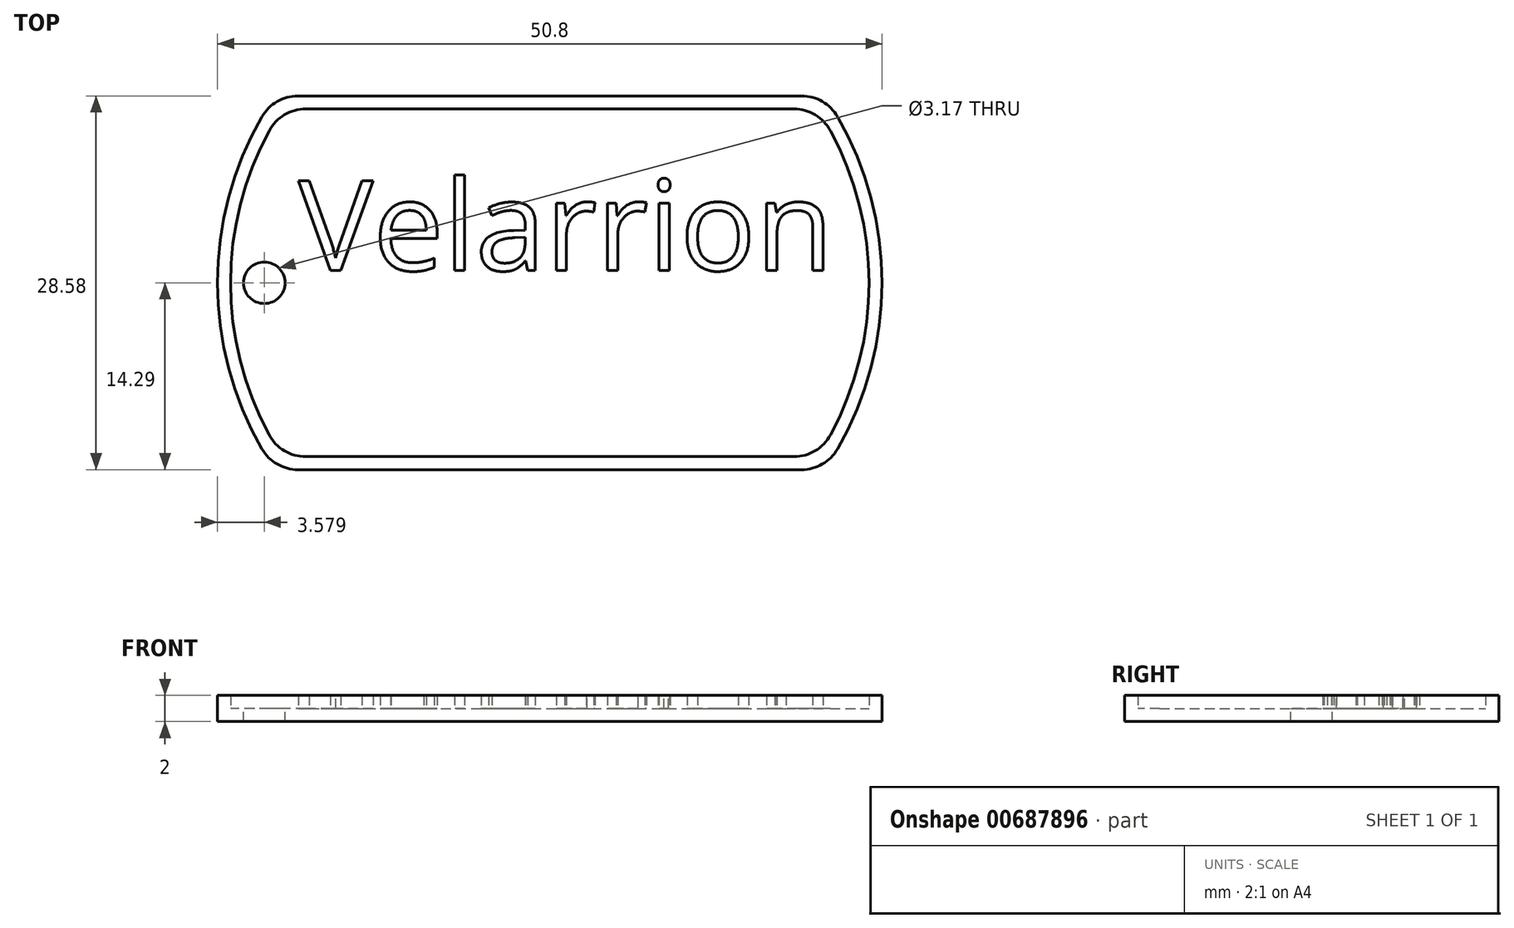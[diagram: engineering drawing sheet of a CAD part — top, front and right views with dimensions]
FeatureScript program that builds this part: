
annotation { "Feature Type Name" : "Feature", "Feature Type Description" : "" }
export const myFeature = defineFeature(function(context is Context, id is Id, definition is map)
    precondition{}
    {
        {
            var Q0;
            Q0=qCreatedBy(makeId("Top.planeOp"),FACE);
            var sketch = newSketch(context, id + "F0", { "sketchPlane" : qUnion([Q0])});
            skArc(sketch, "E0", {"start": v(-22, 12.7) * mm, "mid": v(-25.4, 0) * mm, "end": v(-22, -12.7) * mm});
            skLineSegment(sketch, "E1.top", {"start": v(-19.25, -14.29) * mm, "end": v(19.25, -14.29) * mm});
            skArc(sketch, "E2.trimOffspring", {"start": v(22, -12.7) * mm, "mid": v(25.4, 0) * mm, "end": v(22, 12.7) * mm});
            skLineSegment(sketch, "E3", {"start": v(-19.25, 14.29) * mm, "end": v(19.25, 14.29) * mm});
            skPoint(sketch, "E4.visualSharp", {"position": v(-21, 14.29) * mm});
            skArc(sketch, "E4.filletArc", {"start": v(-19.25, 14.29) * mm, "mid": v(-20.83, 13.86) * mm, "end": v(-22, 12.7) * mm});
            skPoint(sketch, "E5.visualSharp", {"position": v(21, 14.29) * mm});
            skArc(sketch, "E5.filletArc", {"start": v(22, 12.7) * mm, "mid": v(20.83, 13.86) * mm, "end": v(19.25, 14.29) * mm});
            skPoint(sketch, "E6.visualSharp", {"position": v(21, -14.29) * mm});
            skArc(sketch, "E6.filletArc", {"start": v(19.25, -14.29) * mm, "mid": v(20.83, -13.86) * mm, "end": v(22, -12.7) * mm});
            skPoint(sketch, "E7.visualSharp", {"position": v(-21, -14.29) * mm});
            skArc(sketch, "E7.filletArc", {"start": v(-22, -12.7) * mm, "mid": v(-20.83, -13.86) * mm, "end": v(-19.25, -14.29) * mm});
            skSolve(sketch);
        }
        {
            var Q0;
            Q0=makeQuery(id+"F0.imprint","IMPRINT",FACE,{"disambiguationData":[TD([[makeQuery(id+"F0.imprint","IMPRINT",EDGE,{"derivedFrom":sQuery(id+"F0.wireOp",EDGE,"E0")}),1.0]])]});
            extrude(context, id + "F1", {"entities" : qUnion([Q0]), "depth" : 1 * mm, "offsetDistance" : 25.4 * mm});
        }
        {
            var Q0;
            Q0=makeQuery(id+"F1.opExtrude","CAP_FACE",FACE,{"disambiguationData":[OSD([sQuery(id+"F0.wireOp",EDGE,"E0"),sQuery(id+"F0.wireOp",EDGE,"E1.top"),sQuery(id+"F0.wireOp",EDGE,"E2.trimOffspring"),sQuery(id+"F0.wireOp",EDGE,"E3"),sQuery(id+"F0.wireOp",EDGE,"E4.filletArc"),sQuery(id+"F0.wireOp",EDGE,"E5.filletArc"),sQuery(id+"F0.wireOp",EDGE,"E6.filletArc"),sQuery(id+"F0.wireOp",EDGE,"E7.filletArc")])],"isStart":false});
            var sketch = newSketch(context, id + "F2", { "sketchPlane" : qUnion([Q0])});
            skLineSegment(sketch, "E8.0", {"start": v(-18.66, 13.29) * mm, "end": v(18.66, 13.29) * mm});
            skArc(sketch, "E8.1", {"start": v(-21.45, 11.63) * mm, "mid": v(-24.4, 0) * mm, "end": v(-21.45, -11.63) * mm});
            skLineSegment(sketch, "E8.2", {"start": v(-18.66, -13.29) * mm, "end": v(18.66, -13.29) * mm});
            skArc(sketch, "E8.3", {"start": v(21.45, -11.63) * mm, "mid": v(24.4, 0) * mm, "end": v(21.45, 11.63) * mm});
            skPoint(sketch, "E9.visualSharp", {"position": v(-20.46, 13.29) * mm});
            skArc(sketch, "E9.filletArc", {"start": v(-18.66, 13.29) * mm, "mid": v(-20.29, 12.84) * mm, "end": v(-21.45, 11.63) * mm});
            skPoint(sketch, "E10.visualSharp", {"position": v(20.46, 13.29) * mm});
            skArc(sketch, "E10.filletArc", {"start": v(21.45, 11.63) * mm, "mid": v(20.29, 12.84) * mm, "end": v(18.66, 13.29) * mm});
            skPoint(sketch, "E11.visualSharp", {"position": v(20.46, -13.29) * mm});
            skArc(sketch, "E11.filletArc", {"start": v(18.66, -13.29) * mm, "mid": v(20.29, -12.84) * mm, "end": v(21.45, -11.63) * mm});
            skPoint(sketch, "E12.visualSharp", {"position": v(-20.46, -13.29) * mm});
            skArc(sketch, "E12.filletArc", {"start": v(-21.45, -11.63) * mm, "mid": v(-20.29, -12.84) * mm, "end": v(-18.66, -13.29) * mm});
            skLineSegment(sketch, "E13.0", {"start": v(-19.25, 14.29) * mm, "end": v(19.25, 14.29) * mm});
            skArc(sketch, "E13.1", {"start": v(-22, 12.7) * mm, "mid": v(-25.4, 0) * mm, "end": v(-22, -12.7) * mm});
            skLineSegment(sketch, "E13.2", {"start": v(-19.25, -14.29) * mm, "end": v(19.25, -14.29) * mm});
            skArc(sketch, "E13.3", {"start": v(22, -12.7) * mm, "mid": v(25.4, 0) * mm, "end": v(22, 12.7) * mm});
            skPoint(sketch, "E14.visualSharp", {"position": v(-21, -14.29) * mm});
            skArc(sketch, "E14.filletArc", {"start": v(-22, -12.7) * mm, "mid": v(-20.83, -13.86) * mm, "end": v(-19.25, -14.29) * mm});
            skPoint(sketch, "E15.visualSharp", {"position": v(21, -14.29) * mm});
            skArc(sketch, "E15.filletArc", {"start": v(19.25, -14.29) * mm, "mid": v(20.83, -13.86) * mm, "end": v(22, -12.7) * mm});
            skPoint(sketch, "E16.visualSharp", {"position": v(21, 14.29) * mm});
            skArc(sketch, "E16.filletArc", {"start": v(22, 12.7) * mm, "mid": v(20.83, 13.86) * mm, "end": v(19.25, 14.29) * mm});
            skPoint(sketch, "E17.visualSharp", {"position": v(-21, 14.29) * mm});
            skArc(sketch, "E17.filletArc", {"start": v(-19.25, 14.29) * mm, "mid": v(-20.83, 13.86) * mm, "end": v(-22, 12.7) * mm});
            skSolve(sketch);
        }
        {
            var Q0;
            Q0=makeQuery(id+"F2.imprint","IMPRINT",FACE,{"disambiguationData":[TD([[makeQuery(id+"F2.imprint","IMPRINT",EDGE,{"derivedFrom":sQuery(id+"F2.wireOp",EDGE,"E8.0")}),1.0]])]});
            extrude(context, id + "F3", {"entities" : qUnion([Q0]), "operationType" : NewBodyOperationType.ADD, "depth" : 1 * mm, "offsetDistance" : 25.4 * mm});
        }
        {
            var Q0;
            Q0=makeQuery(id+"F1.opExtrude","CAP_FACE",FACE,{"disambiguationData":[OSD([sQuery(id+"F0.wireOp",EDGE,"E0"),sQuery(id+"F0.wireOp",EDGE,"E1.top"),sQuery(id+"F0.wireOp",EDGE,"E2.trimOffspring"),sQuery(id+"F0.wireOp",EDGE,"E3"),sQuery(id+"F0.wireOp",EDGE,"E4.filletArc"),sQuery(id+"F0.wireOp",EDGE,"E5.filletArc"),sQuery(id+"F0.wireOp",EDGE,"E6.filletArc"),sQuery(id+"F0.wireOp",EDGE,"E7.filletArc")])],"isStart":false});
            var sketch = newSketch(context, id + "F4", { "sketchPlane" : qUnion([Q0])});
            skCircle(sketch, "E18", {"center": v(-21.82, 0) * mm, "radius": 1.59 * mm});
            skSolve(sketch);
        }
        {
            var Q0;
            Q0=makeQuery(id+"F4.imprint","IMPRINT",FACE,{"disambiguationData":[TD([[makeQuery(id+"F4.imprint","IMPRINT",EDGE,{"derivedFrom":sQuery(id+"F4.wireOp",EDGE,"E18")}),1.0]])]});
            extrude(context, id + "F5", {"entities" : qUnion([Q0]), "operationType" : NewBodyOperationType.REMOVE, "oppositeDirection" : true, "depth" : 1 * mm, "offsetDistance" : 25.4 * mm});
        }
        {
            var Q0;
            Q0=makeQuery(id+"F2.imprint","IMPRINT",FACE,{"disambiguationData":[TD([[makeQuery(id+"F2.imprint","IMPRINT",EDGE,{"derivedFrom":sQuery(id+"F2.wireOp",EDGE,"E8.0")}),-1.0]])]});
            var sketch = newSketch(context, id + "F6", { "sketchPlane" : qUnion([Q0])});
            skText(sketch, "E19", { "text": "Velarrion", "fontName": "OpenSans-Regular.ttf"});
            const initialGuessF6  = {"E19": [-0.01922, 0.00095, 1, 0, 0.00692]};
            skSetInitialGuess(sketch, initialGuessF6);
            skSolve(sketch);
        }
        {
            var Q0;
            Q0 = qSketchRegion(id + "F6", true);
            extrude(context, id + "F7", {"entities" : qUnion([Q0]), "operationType" : NewBodyOperationType.ADD, "depth" : 1 * mm, "offsetDistance" : 25.4 * mm});
        }
        {
            var Q0;
            Q0 = qSketchRegion(id + "F6", true);
            extrude(context, id + "F8", {"entities" : qUnion([Q0]), "operationType" : NewBodyOperationType.ADD, "depth" : 1 * mm, "offsetDistance" : 25.4 * mm});
        }
    });
